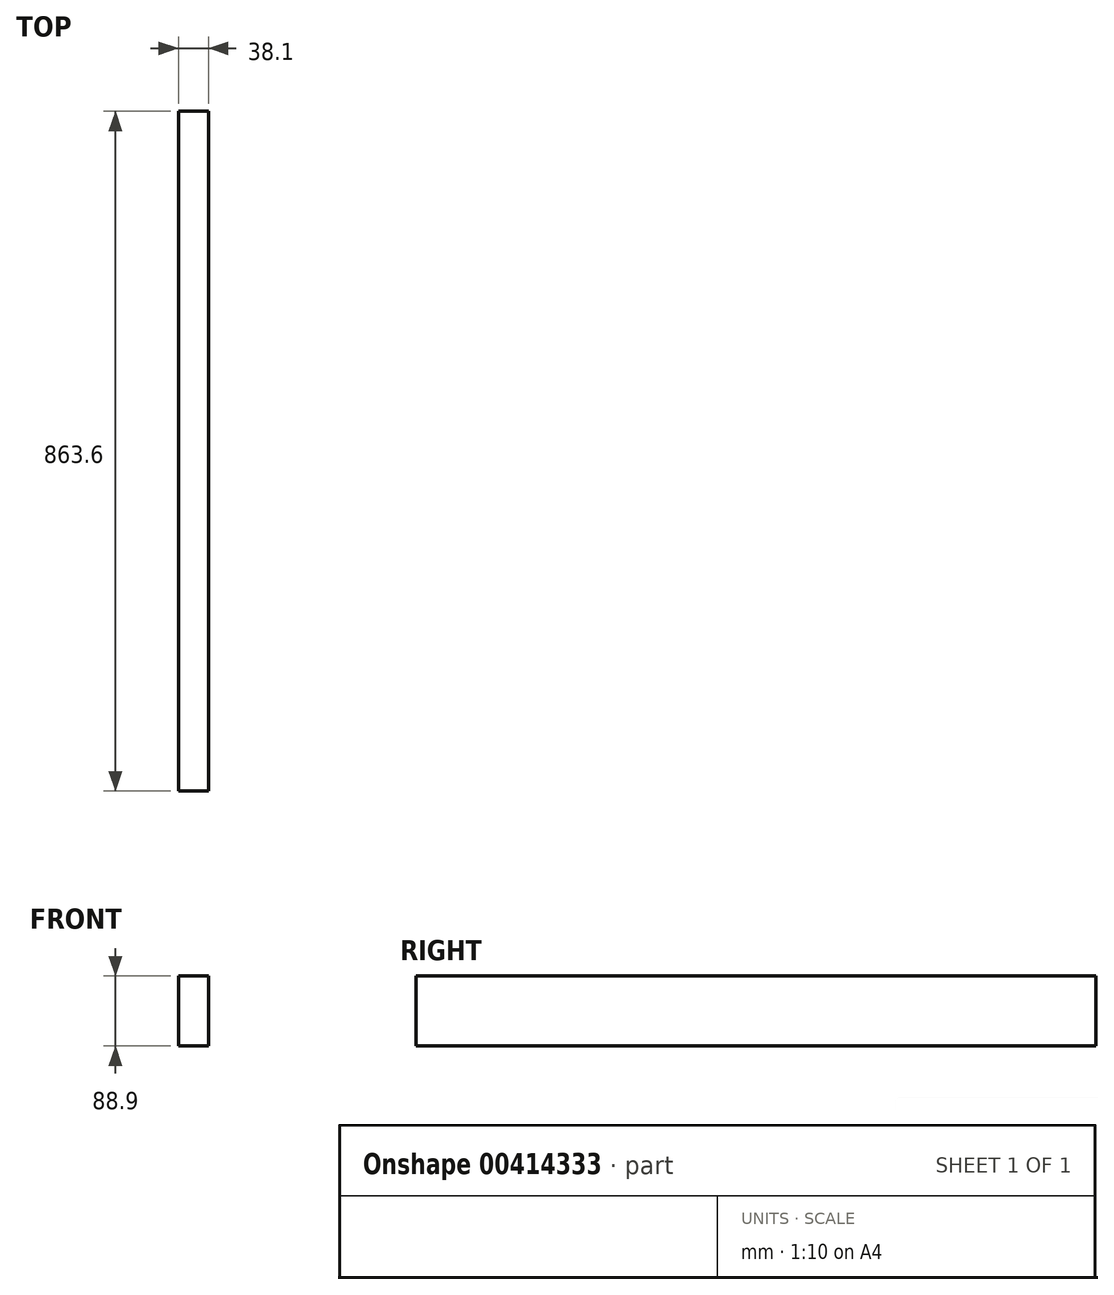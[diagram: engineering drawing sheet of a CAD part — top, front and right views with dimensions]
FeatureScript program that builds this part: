
annotation { "Feature Type Name" : "Feature", "Feature Type Description" : "" }
export const myFeature = defineFeature(function(context is Context, id is Id, definition is map)
    precondition{}
    {
        {
            var Q0;
            Q0=qCreatedBy(makeId("Top.planeOp"),FACE);
            var sketch = newSketch(context, id + "F0", { "sketchPlane" : qUnion([Q0])});
            skLineSegment(sketch, "E0.bottom", {"start": v(-19.05, 431.8) * mm, "end": v(19.05, 431.8) * mm});
            skLineSegment(sketch, "E0.top", {"start": v(-19.05, -431.8) * mm, "end": v(19.05, -431.8) * mm});
            skLineSegment(sketch, "E0.left", {"start": v(-19.05, 431.8) * mm, "end": v(-19.05, -431.8) * mm});
            skLineSegment(sketch, "E0.right", {"start": v(19.05, 431.8) * mm, "end": v(19.05, -431.8) * mm});
            skPoint(sketch, "E0.middle", {"position": v(0, 0) * mm});
            skSolve(sketch);
        }
        {
            var Q0;
            Q0 = qSketchRegion(id + "F0", true);
            extrude(context, id + "F1", {"entities" : qUnion([Q0]), "depth" : 88.9 * mm});
        }
    });
